# Revit family: PRD_AR_TpsAndWtrSpplOtltFttngs_FittingUnit_AQFU0226-AQFU0229 2
name_source: partatom
category: Plumbing Fixtures
units: mm (PartAtom-declared; Revit-internal decimal feet)

## family parameters
Cut with Voids When Loaded = No
Enable Cutting in Views = No
Host = Face
Maintain Annotation Orientation = No
OmniClass Number = 23.45.55.11
OmniClass Title = Sanitary Components
Part Type = Normal
Room Calculation Point = No
Round Connector Dimension = Use Diameter
Shared = No

## types (4) — shared parameters
AssetType = Fixed
BodyMaterial = PRD_AR_StainlessSteel_SatinFinished
Category = Pr_40_20_87, Taps and water supply outlet fittings
Circulation = no
Default Elevation = 1050 mm
Export Type to IFC As = IfcDistributionChamberElementType
Finish = satin finished
Fitting = separately
FlowColdWater = 0.0 L/s
FlowHotWater = 0.0 L/s
HygieneFlushing = no
IfcExportAs = IfcDistributionChamberElement
IfcExportType = USERDEFINED
InletConversionSize = 20  [stored 0.0656168 ft]
InletSize = G 3/4
Manufacturer = KWC Group Management AG
ManufacturerName = KWC Group Management AG
ManufacturerURL = www.kwc-professional.com
Material = stainless steel
NominalDepth = 72 mm  [stored 0.23622 ft]
NominalHeight = 173 mm  [stored 0.567585 ft]
OutletSize = 15  [stored 0.0492126 ft]
OverallDepth = 72 mm
OverallHeight = 173 mm
PositionOfWaterConnection = from backside
ProductInformation = http://pim.kwc.com
Status = New
Type IFC Predefined Type = USERDEFINED
TypeOfMixing = yes
TypeOfMounting = wall mounting
URL = www.kwc-professional.com
Uniclass2015Code = Pr_40_20_87
Uniclass2015Title = Taps and water supply outlet fittings
Uniclass2015Version = Products v1.38
Version = 1
WashPlaceWidth = 800 mm

## per-type parameters (varying)
| type | BIMObjectName | Description | Features | HalfWidth | ModelNumber | Name | NominalWidth | NumberOfWashPlaces | OverallWidth | Size | Width |
| AQFU0226 | PRD_AR_TapsAndWaterSupplyOutletFittings_FittingUnit_AQFU0226 | Fitting unit ready for connection with 2 wash places, for wall mounting, for connection to hot and cold water from right or left at rear. Housing made of stainless steel, satin finished with pre-assembled fitting connection blocks and connection options for power supply to electronic fittings, stainless steel piping, hanging rail and mounting materials. | With 2 wash places, housing width 1600 mm. Wash place width 800 mm. | 800 mm  [stored 2.62467 ft] | 2030064918 | Fitting unit for wall mounting AQFU0226 | 1600 mm  [stored 5.24934 ft] | 2 | 1,600 mm | 1600 x 173 x 72 mm (W x H x D) | 1600 mm  [stored 5.24934 ft] |
| AQFU0227 | PRD_AR_TapsAndWaterSupplyOutletFittings_FittingUnit_AQFU0227 | Fitting unit ready for connection with 3 wash places, for wall mounting, for connection to hot and cold water from right or left at rear. Housing made of stainless steel, satin finished with pre-assembled fitting connection blocks and connection options for power supply to electronic fittings, stainless steel piping, hanging rail and mounting materials. | With 3 wash places, housing width 2400 mm. Wash place width 800 mm. | 1200 mm | 2030064919 | Fitting unit for wall mounting AQFU0227 | 2400 mm | 3 | 2,400 mm | 2400 x 173 x 72 mm (W x H x D) | 2400 mm |
| AQFU0228 | PRD_AR_TapsAndWaterSupplyOutletFittings_FittingUnit_AQFU0228 | Fitting unit ready for connection with 4 wash places, for wall mounting, for connection to hot and cold water from right or left at rear. Housing made of stainless steel, satin finished with pre-assembled fitting connection blocks and connection options for power supply to electronic fittings, stainless steel piping, hanging rail and mounting materials. | With 4 wash places, housing width 3200 mm. Wash place width 800 mm. | 1600 mm  [stored 5.24934 ft] | 2030064920 | Fitting unit for wall mounting AQFU0228 | 3200 mm  [stored 10.4987 ft] | 4 | 3,200 mm | 3200 x 173 x 72 mm (W x H x D) | 3200 mm  [stored 10.4987 ft] |
| AQFU0229 | PRD_AR_TapsAndWaterSupplyOutletFittings_FittingUnit_AQFU0229 | Fitting unit ready for connection with 5 wash places, for wall mounting, for connection to hot and cold water from right or left at rear. Housing made of stainless steel, satin finished with pre-assembled fitting connection blocks and connection options for power supply to electronic fittings, stainless steel piping, hanging rail and mounting materials. | With 5 wash places, housing width 4000 mm. Wash place width 800 mm. | 2000 mm  [stored 6.56168 ft] | 2030064921 | Fitting unit for wall mounting AQFU0229 | 4000 mm  [stored 13.1234 ft] | 5 | 4,000 mm | 4000 x 173 x 72 mm (W x H x D) | 4000 mm  [stored 13.1234 ft] |

note: column(s) folded — value = type name in every type: Model, ModelReference

note: [stored X ft] marks values corroborated as IEEE doubles in the binary element streams (Revit-internal decimal feet)

## geometry (parser evidence)
native form markers: Sweep x4
no freeform markers — native parametric forms only
